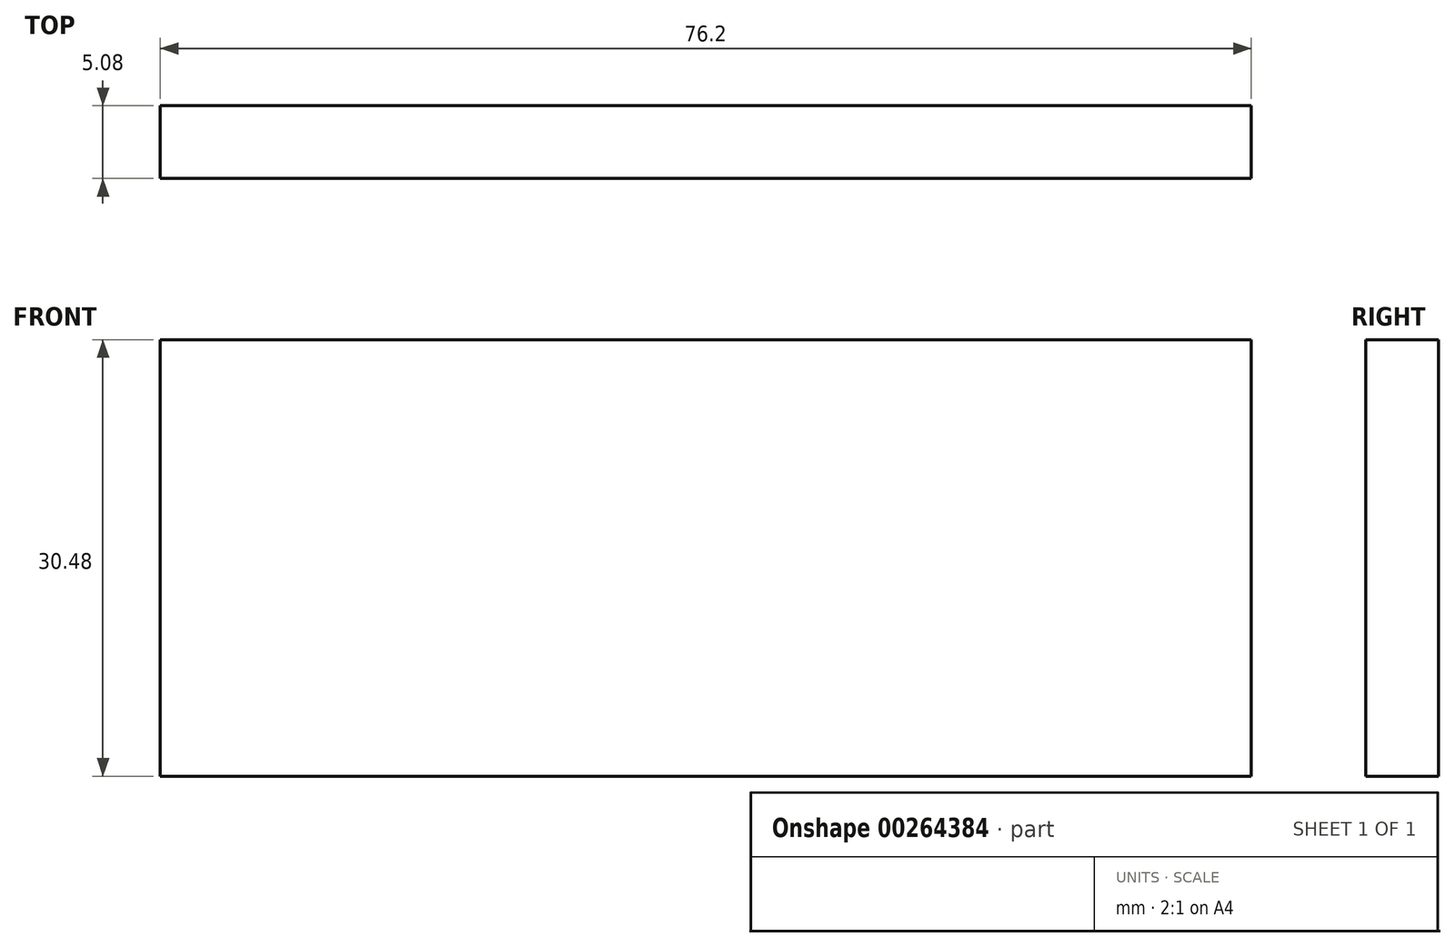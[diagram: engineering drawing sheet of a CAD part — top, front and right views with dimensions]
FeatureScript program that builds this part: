
annotation { "Feature Type Name" : "Feature", "Feature Type Description" : "" }
export const myFeature = defineFeature(function(context is Context, id is Id, definition is map)
    precondition{}
    {
        {
            var Q0;
            Q0=qCreatedBy(makeId("Front.planeOp"),FACE);
            var sketch = newSketch(context, id + "F0", { "sketchPlane" : qUnion([Q0])});
            skLineSegment(sketch, "E0.bottom", {"start": v(-64.1, 49.5) * mm, "end": v(12.1, 49.5) * mm});
            skLineSegment(sketch, "E0.top", {"start": v(-64.1, 19.02) * mm, "end": v(12.1, 19.02) * mm});
            skLineSegment(sketch, "E0.left", {"start": v(-64.1, 49.5) * mm, "end": v(-64.1, 19.02) * mm});
            skLineSegment(sketch, "E0.right", {"start": v(12.1, 49.5) * mm, "end": v(12.1, 19.02) * mm});
            skSolve(sketch);
        }
        {
            var Q0;
            Q0 = qSketchRegion(id + "F0", true);
            extrude(context, id + "F1", {"entities" : qUnion([Q0]), "depth" : 5.08 * mm});
        }
    });
